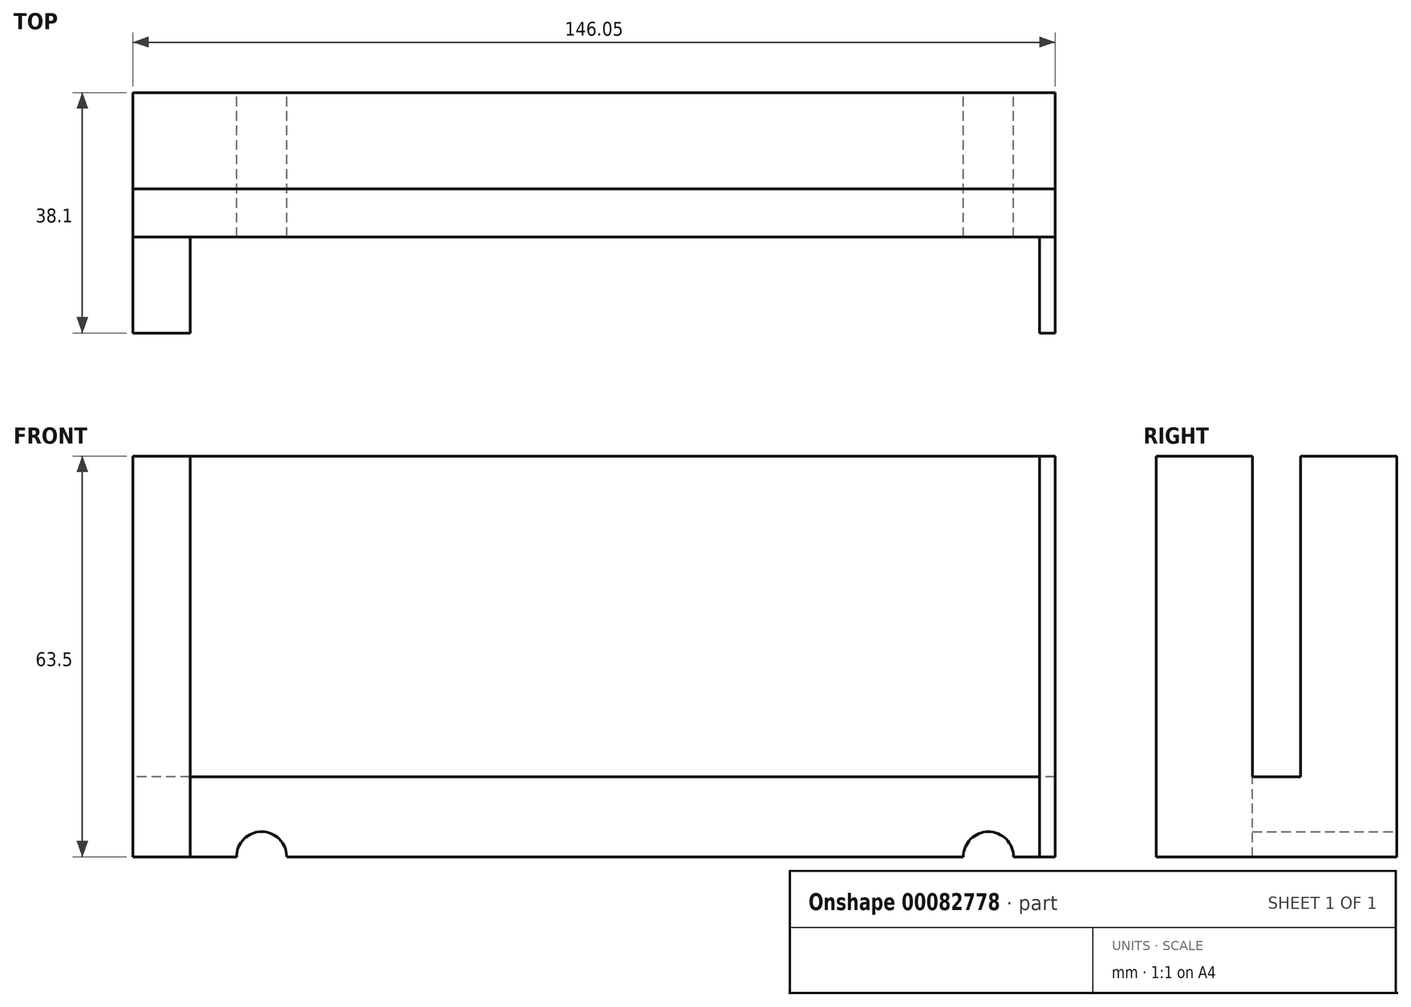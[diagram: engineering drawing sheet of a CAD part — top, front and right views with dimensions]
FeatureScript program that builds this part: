
annotation { "Feature Type Name" : "Feature", "Feature Type Description" : "" }
export const myFeature = defineFeature(function(context is Context, id is Id, definition is map)
    precondition{}
    {
        {
            var Q0;
            Q0=qCreatedBy(makeId("Front.planeOp"),FACE);
            var sketch = newSketch(context, id + "F0", { "sketchPlane" : qUnion([Q0])});
            skLineSegment(sketch, "E0", {"start": v(-90.83, -33.59) * mm, "end": v(55.22, -33.59) * mm});
            skLineSegment(sketch, "E1", {"start": v(55.22, -33.59) * mm, "end": v(55.22, -8.19) * mm});
            skLineSegment(sketch, "E2", {"start": v(55.22, -8.19) * mm, "end": v(-90.83, -8.19) * mm});
            skLineSegment(sketch, "E3", {"start": v(-90.83, -8.19) * mm, "end": v(-90.83, -33.59) * mm});
            skSolve(sketch);
        }
        {
            var Q0;
            Q0 = qSketchRegion(id + "F0", true);
            extrude(context, id + "F1", {"entities" : qUnion([Q0]), "depth" : 38.1 * mm});
        }
        {
            var Q0;
            Q0=makeQuery(id+"F1.opExtrude","SWEPT_FACE",FACE,{"disambiguationData":[OSD([sQuery(id+"F0.wireOp",EDGE,"E3")])]});
            var sketch = newSketch(context, id + "F2", { "sketchPlane" : qUnion([Q0])});
            skLineSegment(sketch, "E4", {"start": v(15.24, -20.89) * mm, "end": v(15.24, -8.19) * mm});
            skLineSegment(sketch, "E5", {"start": v(15.24, -8.19) * mm, "end": v(22.86, -8.19) * mm});
            skLineSegment(sketch, "E6", {"start": v(22.86, -8.19) * mm, "end": v(22.86, -20.89) * mm});
            skLineSegment(sketch, "E7", {"start": v(22.86, -20.89) * mm, "end": v(15.24, -20.89) * mm});
            skPoint(sketch, "E8.start.orphan", {"position": v(0, -20.89) * mm});
            skPoint(sketch, "E9.start.orphan", {"position": v(38.1, -20.89) * mm});
            skSolve(sketch);
        }
        {
            var Q0;
            Q0 = qSketchRegion(id + "F2", true);
            var Q1;
            Q1=makeQuery(id+"F1.opExtrude","SWEPT_FACE",FACE,{"disambiguationData":[OSD([sQuery(id+"F0.wireOp",EDGE,"E1")])]});
            extrude(context, id + "F3", {"entities" : qUnion([Q0, Q1]), "operationType" : NewBodyOperationType.REMOVE, "endBound" : BoundingType.THROUGH_ALL, "oppositeDirection" : true, "depth" : 25.4 * mm});
        }
        {
            var Q0;
            {var subQ1=sQuery(id+"F0.wireOp",EDGE,"E2");Q0=makeQuery(id+"F3.boolean.opBoolean","SPLIT",FACE,{"disambiguationData":[TD([makeQuery(id+"F3.opExtrude","SWEPT_FACE",FACE,{"disambiguationData":[OSD([sQuery(id+"F2.wireOp",EDGE,"E6")])]})])],"derivedFrom":makeQuery(id+"F1.opExtrude","SWEPT_FACE",FACE,{"disambiguationData":[OSD([subQ1])]})});}
            var sketch = newSketch(context, id + "F4", { "sketchPlane" : qUnion([Q0])});
            skLineSegment(sketch, "E10", {"start": v(-81.77, -22.86) * mm, "end": v(-81.77, -38.1) * mm});
            skLineSegment(sketch, "E11", {"start": v(52.77, -30.48) * mm, "end": v(52.77, -38.1) * mm});
            skLineSegment(sketch, "E12", {"start": v(52.77, -30.48) * mm, "end": v(52.77, -22.86) * mm});
            skLineSegment(sketch, "E13", {"start": v(-81.77, -22.86) * mm, "end": v(52.77, -22.86) * mm});
            skLineSegment(sketch, "E14", {"start": v(-81.77, -38.1) * mm, "end": v(52.77, -38.1) * mm});
            skSolve(sketch);
        }
        {
            var Q0;
            Q0 = qSketchRegion(id + "F4", true);
            extrude(context, id + "F5", {"entities" : qUnion([Q0]), "operationType" : NewBodyOperationType.REMOVE, "endBound" : BoundingType.THROUGH_ALL, "oppositeDirection" : true, "depth" : 26.18 * mm});
        }
        {
            var Q0;
            {var subQ1=sQuery(id+"F0.wireOp",EDGE,"E2");Q0=makeQuery(id+"F3.boolean.opBoolean","SPLIT",FACE,{"disambiguationData":[TD([makeQuery(id+"F3.opExtrude","SWEPT_FACE",FACE,{"disambiguationData":[OSD([sQuery(id+"F2.wireOp",EDGE,"E4")])]})])],"derivedFrom":makeQuery(id+"F1.opExtrude","SWEPT_FACE",FACE,{"disambiguationData":[OSD([subQ1])]})});}
            var sketch = newSketch(context, id + "F6", { "sketchPlane" : qUnion([Q0])});
            skLineSegment(sketch, "E15", {"start": v(-90.83, 0) * mm, "end": v(55.22, 0) * mm});
            skLineSegment(sketch, "E16", {"start": v(55.22, 0) * mm, "end": v(55.22, -15.24) * mm});
            skLineSegment(sketch, "E17", {"start": v(55.22, -15.24) * mm, "end": v(-90.83, -15.24) * mm});
            skLineSegment(sketch, "E18", {"start": v(-90.83, -15.24) * mm, "end": v(-90.83, 0) * mm});
            skSolve(sketch);
        }
        {
            var Q0;
            Q0 = qSketchRegion(id + "F6", true);
            extrude(context, id + "F7", {"entities" : qUnion([Q0]), "operationType" : NewBodyOperationType.ADD, "depth" : 38.1 * mm});
        }
        {
            var Q0;
            {var subQ0=sQuery(id+"F0.wireOp",EDGE,"E3");var subQ1=sQuery(id+"F0.wireOp",EDGE,"E2");var subQ4=makeQuery(id+"F1.opExtrude","SWEPT_FACE",FACE,{"disambiguationData":[OSD([subQ0])]});var subQ5=makeQuery(id+"F3.opExtrude","SWEPT_FACE",FACE,{"disambiguationData":[OSD([sQuery(id+"F2.wireOp",EDGE,"E6")])]});Q0=makeQuery(id+"F5.boolean.opBoolean","SPLIT",FACE,{"disambiguationData":[TD([subQ4])],"derivedFrom":makeQuery(id+"F3.boolean.opBoolean","SPLIT",FACE,{"disambiguationData":[TD([subQ5])],"derivedFrom":makeQuery(id+"F1.opExtrude","SWEPT_FACE",FACE,{"disambiguationData":[OSD([subQ1])]})})});}
            var sketch = newSketch(context, id + "F8", { "sketchPlane" : qUnion([Q0])});
            skLineSegment(sketch, "E19", {"start": v(-90.83, -38.1) * mm, "end": v(-90.83, -22.86) * mm});
            skLineSegment(sketch, "E20", {"start": v(-90.83, -22.86) * mm, "end": v(-81.77, -22.86) * mm});
            skLineSegment(sketch, "E21", {"start": v(-81.77, -22.86) * mm, "end": v(-81.77, -38.1) * mm});
            skLineSegment(sketch, "E22", {"start": v(-81.77, -38.1) * mm, "end": v(-90.83, -38.1) * mm});
            skSolve(sketch);
        }
        {
            var Q0;
            Q0 = qSketchRegion(id + "F8", true);
            extrude(context, id + "F9", {"entities" : qUnion([Q0]), "operationType" : NewBodyOperationType.ADD, "depth" : 38.1 * mm});
        }
        {
            var Q0;
            {var subQ1=sQuery(id+"F0.wireOp",EDGE,"E2");var subQ2=sQuery(id+"F0.wireOp",EDGE,"E1");var subQ4=makeQuery(id+"F1.opExtrude","SWEPT_FACE",FACE,{"disambiguationData":[OSD([subQ2])]});var subQ5=makeQuery(id+"F3.opExtrude","SWEPT_FACE",FACE,{"disambiguationData":[OSD([sQuery(id+"F2.wireOp",EDGE,"E6")])]});Q0=makeQuery(id+"F5.boolean.opBoolean","SPLIT",FACE,{"disambiguationData":[TD([subQ4])],"derivedFrom":makeQuery(id+"F3.boolean.opBoolean","SPLIT",FACE,{"disambiguationData":[TD([subQ5])],"derivedFrom":makeQuery(id+"F1.opExtrude","SWEPT_FACE",FACE,{"disambiguationData":[OSD([subQ1])]})})});}
            var sketch = newSketch(context, id + "F10", { "sketchPlane" : qUnion([Q0])});
            skLineSegment(sketch, "E23", {"start": v(52.77, -38.1) * mm, "end": v(52.77, -22.86) * mm});
            skLineSegment(sketch, "E24", {"start": v(52.77, -22.86) * mm, "end": v(55.22, -22.86) * mm});
            skLineSegment(sketch, "E25", {"start": v(55.22, -22.86) * mm, "end": v(55.22, -38.1) * mm});
            skLineSegment(sketch, "E26", {"start": v(55.22, -38.1) * mm, "end": v(52.77, -38.1) * mm});
            skSolve(sketch);
        }
        {
            var Q0;
            Q0 = qSketchRegion(id + "F10", true);
            extrude(context, id + "F11", {"entities" : qUnion([Q0]), "operationType" : NewBodyOperationType.ADD, "depth" : 38.1 * mm});
        }
        {
            var Q0;
            Q0=makeQuery(id+"F7.boolean.opBoolean","MERGE",FACE,{"derivedFrom":[makeQuery(id+"F1.opExtrude","CAP_FACE",FACE,{"disambiguationData":[OSD([sQuery(id+"F0.wireOp",EDGE,"E0"),sQuery(id+"F0.wireOp",EDGE,"E1"),sQuery(id+"F0.wireOp",EDGE,"E2"),sQuery(id+"F0.wireOp",EDGE,"E3")])],"isStart":true}),makeQuery(id+"F7.opExtrude","SWEPT_FACE",FACE,{"disambiguationData":[OSD([sQuery(id+"F6.wireOp",EDGE,"E15")])]})]});
            var sketch = newSketch(context, id + "F12", { "sketchPlane" : qUnion([Q0])});
            skCircle(sketch, "E27", {"center": v(-44.65, -33.59) * mm, "radius": 3.97 * mm});
            skLineSegment(sketch, "E28", {"start": v(66.47, -33.59) * mm, "end": v(70.44, -33.59) * mm});
            skCircle(sketch, "E29", {"center": v(70.44, -33.59) * mm, "radius": 3.98 * mm});
            skSolve(sketch);
        }
        {
            var Q0;
            Q0 = qSketchRegion(id + "F12", true);
            extrude(context, id + "F13", {"entities" : qUnion([Q0]), "operationType" : NewBodyOperationType.REMOVE, "endBound" : BoundingType.THROUGH_ALL, "oppositeDirection" : true, "depth" : 25.4 * mm});
        }
    });
